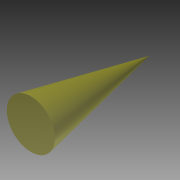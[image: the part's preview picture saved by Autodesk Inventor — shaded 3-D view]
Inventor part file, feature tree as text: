
AUTODESK INVENTOR PART (.ipt)
format: ipt  version: 2015 (Build 190159000, 159)  size: 82,944 bytes
history: native  units: mm
features: revolve x1, other x1, sketch x1
ambient origin geometry x8: Origin, YZ Plane, XZ Plane, XY Plane, X Axis, Y Axis, Z Axis, Center Point
bodies: Solid1 (feature_tree)
feature tree (3):
  revolve  "Revolution1"  [1 undecoded]
  other  "Work Point1"
  sketch  "Sketch1"  dims[d0=2.007129mm d1=275.0mm d2=90.0deg d3=29.695mm]
note: 1 required parameter value undecoded (feature->parameter linkage not recoverable at this tier; creation-order binding heuristic only, values carry confidence <= 0.55)
